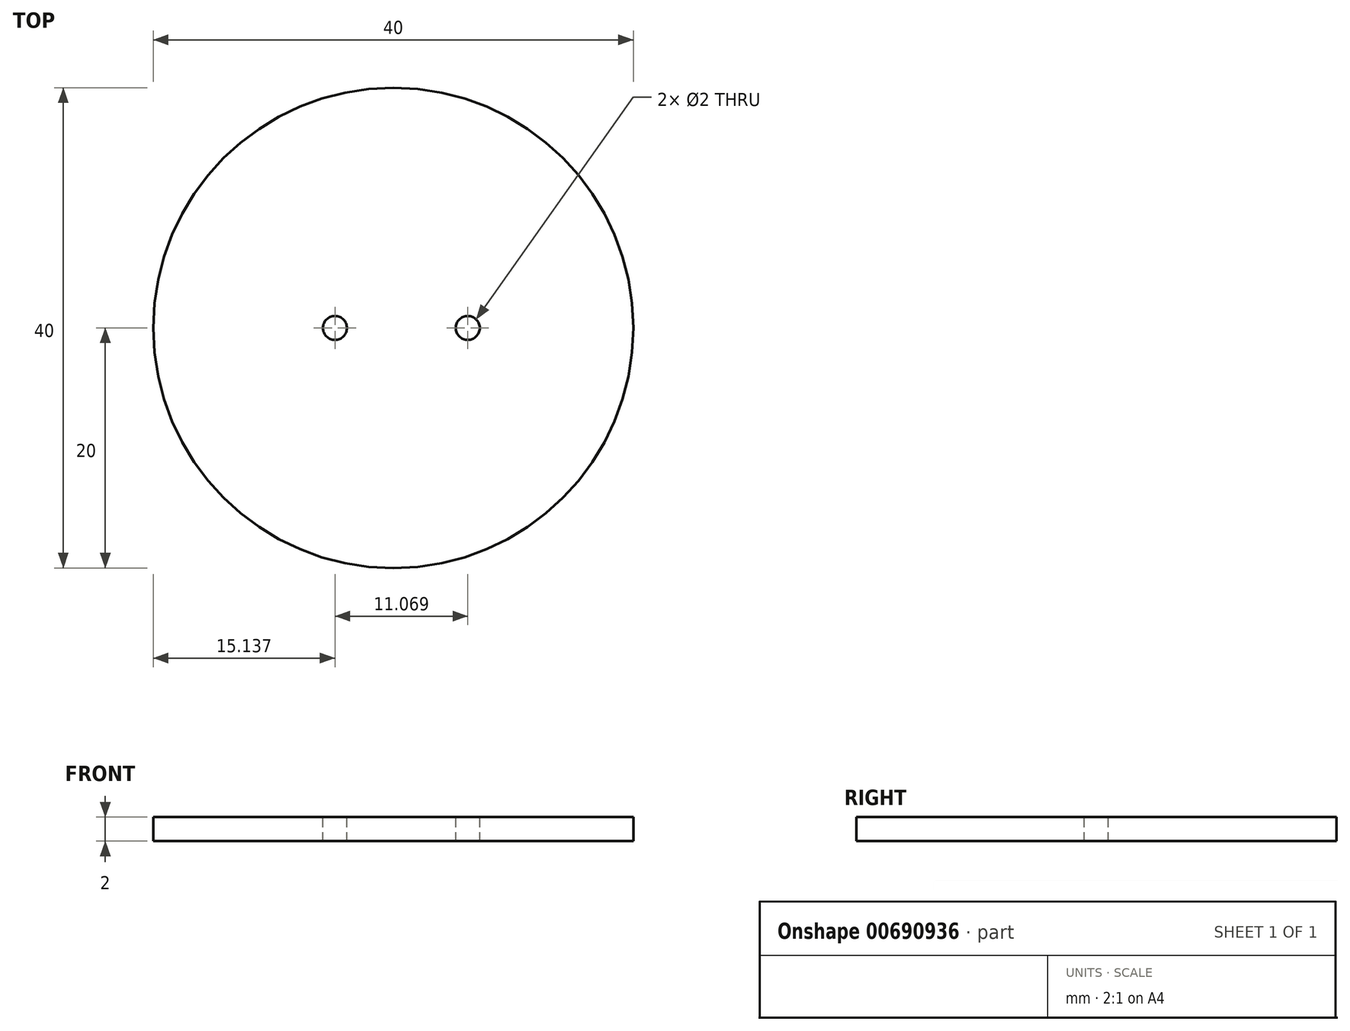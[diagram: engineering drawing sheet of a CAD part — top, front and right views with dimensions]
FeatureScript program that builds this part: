
annotation { "Feature Type Name" : "Feature", "Feature Type Description" : "" }
export const myFeature = defineFeature(function(context is Context, id is Id, definition is map)
    precondition{}
    {
        {
            var Q0;
            Q0=qCreatedBy(makeId("Top.planeOp"),FACE);
            var sketch = newSketch(context, id + "F0", { "sketchPlane" : qUnion([Q0])});
            skCircle(sketch, "E0", {"center": v(0, 0) * mm, "radius": 20 * mm});
            skSolve(sketch);
        }
        {
            var Q0;
            Q0 = qSketchRegion(id + "F0", true);
            extrude(context, id + "F1", {"entities" : qUnion([Q0]), "depth" : 2 * mm, "offsetDistance" : 25 * mm});
        }
        {
            var Q0;
            Q0=makeQuery(id+"F1.opExtrude","CAP_FACE",FACE,{"disambiguationData":[OSD([sQuery(id+"F0.wireOp",EDGE,"E0")])],"isStart":false});
            var sketch = newSketch(context, id + "F2", { "sketchPlane" : qUnion([Q0])});
            skCircle(sketch, "E1", {"center": v(-4.86, 0) * mm, "radius": 1 * mm});
            skCircle(sketch, "E2", {"center": v(6.2, 0) * mm, "radius": 1 * mm});
            skSolve(sketch);
        }
        {
            var Q0;
            Q0 = qSketchRegion(id + "F2", true);
            extrude(context, id + "F3", {"entities" : qUnion([Q0]), "operationType" : NewBodyOperationType.REMOVE, "oppositeDirection" : true, "depth" : 25 * mm, "offsetDistance" : 25 * mm});
        }
    });
